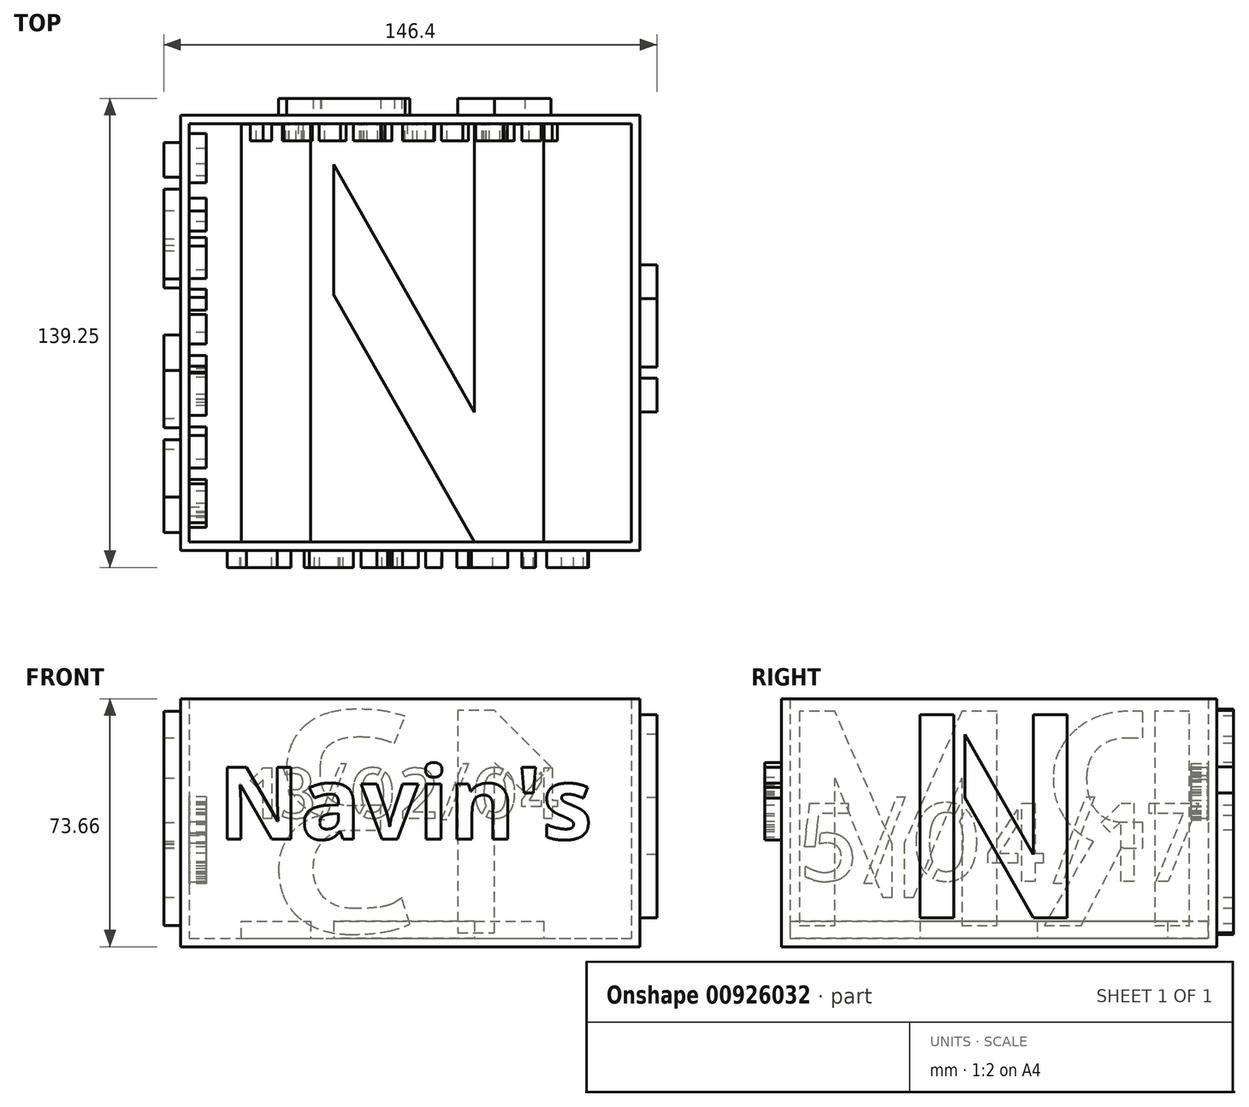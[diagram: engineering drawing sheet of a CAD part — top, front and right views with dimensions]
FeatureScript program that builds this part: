
annotation { "Feature Type Name" : "Feature", "Feature Type Description" : "" }
export const myFeature = defineFeature(function(context is Context, id is Id, definition is map)
    precondition{}
    {
        {
            var Q0;
            Q0=qCreatedBy(makeId("Top.planeOp"),FACE);
            var sketch = newSketch(context, id + "F0", { "sketchPlane" : qUnion([Q0])});
            skLineSegment(sketch, "E0.bottom", {"start": v(-70.44, 64.66) * mm, "end": v(65.96, 64.66) * mm});
            skLineSegment(sketch, "E0.top", {"start": v(-70.44, -64.6) * mm, "end": v(65.96, -64.6) * mm});
            skLineSegment(sketch, "E0.left", {"start": v(-70.44, 64.66) * mm, "end": v(-70.44, -64.6) * mm});
            skLineSegment(sketch, "E0.right", {"start": v(65.96, 64.66) * mm, "end": v(65.96, -64.6) * mm});
            skSolve(sketch);
        }
        {
            var Q0;
            Q0=makeQuery(id+"F0.imprint","IMPRINT",FACE,{"disambiguationData":[TD([[makeQuery(id+"F0.imprint","IMPRINT",EDGE,{"derivedFrom":sQuery(id+"F0.wireOp",EDGE,"E0.bottom")}),-1.0]])]});
            extrude(context, id + "F1", {"entities" : qUnion([Q0]), "depth" : 73.66 * mm, "offsetDistance" : 25.4 * mm});
        }
        {
            var Q0;
            Q0=makeQuery(id+"F1.opExtrude","CAP_FACE",FACE,{"disambiguationData":[OSD([sQuery(id+"F0.wireOp",EDGE,"E0.bottom"),sQuery(id+"F0.wireOp",EDGE,"E0.top"),sQuery(id+"F0.wireOp",EDGE,"E0.left"),sQuery(id+"F0.wireOp",EDGE,"E0.right")])],"isStart":false});
            shell(context, id + "F2", {"entities" : qUnion([Q0]), "thickness" : 2.54 * mm});
        }
        {
            var Q0;
            Q0=makeQuery(id+"F1.opExtrude","SWEPT_FACE",FACE,{"disambiguationData":[OSD([sQuery(id+"F0.wireOp",EDGE,"E0.top")])]});
            var sketch = newSketch(context, id + "F3", { "sketchPlane" : qUnion([Q0])});
            skText(sketch, "E1", { "text": "Navin\'s", "fontName": "OpenSans-Bold.ttf"});
            const initialGuessF3  = {"E1": [-0.0593, 0.03196, 1, 0, 0.02155]};
            skSetInitialGuess(sketch, initialGuessF3);
            skSolve(sketch);
        }
        {
            var Q0;
            Q0 = qSketchRegion(id + "F3", true);
            extrude(context, id + "F4", {"entities" : qUnion([Q0]), "operationType" : NewBodyOperationType.ADD, "depth" : 5 * mm, "offsetDistance" : 25.4 * mm});
        }
        {
            var Q0;
            Q0=makeQuery(id+"F2.opShell","OFFSET_FACE",FACE,{"disambiguationData":[OSD([sQuery(id+"F0.wireOp",EDGE,"E0.bottom"),sQuery(id+"F0.wireOp",EDGE,"E0.top"),sQuery(id+"F0.wireOp",EDGE,"E0.left"),sQuery(id+"F0.wireOp",EDGE,"E0.right")])]});
            var sketch = newSketch(context, id + "F5", { "sketchPlane" : qUnion([Q0])});
            skText(sketch, "E2", { "text": "N", "fontName": "AllertaStencil-Regular.ttf"});
            const initialGuessF5  = {"E2": [-0.0679, -0.06205, 1, 0, 0.12417]};
            skSetInitialGuess(sketch, initialGuessF5);
            skSolve(sketch);
        }
        {
            var Q0;
            Q0 = qSketchRegion(id + "F5", true);
            extrude(context, id + "F6", {"entities" : qUnion([Q0]), "operationType" : NewBodyOperationType.ADD, "depth" : 5 * mm, "offsetDistance" : 25.4 * mm});
        }
        {
            var Q0;
            Q0=makeQuery(id+"F1.opExtrude","SWEPT_FACE",FACE,{"disambiguationData":[OSD([sQuery(id+"F0.wireOp",EDGE,"E0.right")])]});
            var sketch = newSketch(context, id + "F7", { "sketchPlane" : qUnion([Q0])});
            skText(sketch, "E3", { "text": "N", "fontName": "AllertaStencil-Regular.ttf"});
            const initialGuessF7  = {"E3": [-0.03094, 0.00857, 1, 0, 0.06038]};
            skSetInitialGuess(sketch, initialGuessF7);
            skSolve(sketch);
        }
        {
            var Q0;
            Q0 = qSketchRegion(id + "F7", true);
            extrude(context, id + "F8", {"entities" : qUnion([Q0]), "operationType" : NewBodyOperationType.ADD, "depth" : 5 * mm, "offsetDistance" : 25.4 * mm});
        }
        {
            var Q0;
            Q0=makeQuery(id+"F1.opExtrude","SWEPT_FACE",FACE,{"disambiguationData":[OSD([sQuery(id+"F0.wireOp",EDGE,"E0.bottom")])]});
            var sketch = newSketch(context, id + "F9", { "sketchPlane" : qUnion([Q0])});
            skText(sketch, "E4", { "text": "13 ", "fontName": "AllertaStencil-Regular.ttf"});
            const initialGuessF9  = {"E4": [-0.04212, 0.0041, 1, 0, 0.0661]};
            skSetInitialGuess(sketch, initialGuessF9);
            skSolve(sketch);
        }
        {
            var Q0;
            Q0=makeQuery(id+"F9.imprint","IMPRINT",FACE,{"disambiguationData":[TD([[makeQuery(id+"F9.imprint","IMPRINT",EDGE,{"derivedFrom":sQuery(id+"F9.wireOp",EDGE,"E4.sketch_text.stroke-7")}),-1.0]])]});
            var Q1;
            Q1=makeQuery(id+"F9.imprint","IMPRINT",FACE,{"disambiguationData":[TD([[makeQuery(id+"F9.imprint","IMPRINT",EDGE,{"derivedFrom":sQuery(id+"F9.wireOp",EDGE,"E4.sketch_text.stroke-0")}),-1.0]])]});
            extrude(context, id + "F10", {"entities" : qUnion([Q0, Q1]), "operationType" : NewBodyOperationType.ADD, "depth" : 5 * mm, "offsetDistance" : 25.4 * mm});
        }
        {
            var Q0;
            Q0=makeQuery(id+"F1.opExtrude","SWEPT_FACE",FACE,{"disambiguationData":[OSD([sQuery(id+"F0.wireOp",EDGE,"E0.left")])]});
            var sketch = newSketch(context, id + "F11", { "sketchPlane" : qUnion([Q0])});
            skText(sketch, "E5", { "text": "RM", "fontName": "AllertaStencil-Regular.ttf"});
            const initialGuessF11  = {"E5": [-0.06437, 0.00633, 1, 0, 0.06361]};
            skSetInitialGuess(sketch, initialGuessF11);
            skSolve(sketch);
        }
        {
            var Q0;
            Q0 = qSketchRegion(id + "F11", true);
            extrude(context, id + "F12", {"entities" : qUnion([Q0]), "operationType" : NewBodyOperationType.ADD, "depth" : 5 * mm, "offsetDistance" : 25.4 * mm});
        }
        {
            var Q0;
            Q0=makeQuery(id+"F2.opShell","OFFSET_FACE",FACE,{"disambiguationData":[OSD([sQuery(id+"F0.wireOp",EDGE,"E0.bottom")])]});
            var sketch = newSketch(context, id + "F13", { "sketchPlane" : qUnion([Q0])});
            skText(sketch, "E6", { "text": "13/02/04", "fontName": "AllertaStencil-Regular.ttf"});
            const initialGuessF13  = {"E6": [-0.05037, 0.03808, 1, 0, 0.01504]};
            skSetInitialGuess(sketch, initialGuessF13);
            skSolve(sketch);
        }
        {
            var Q0;
            Q0 = qSketchRegion(id + "F13", true);
            extrude(context, id + "F14", {"entities" : qUnion([Q0]), "operationType" : NewBodyOperationType.ADD, "depth" : 5 * mm, "offsetDistance" : 25.4 * mm});
        }
        {
            var Q0;
            Q0=makeQuery(id+"F2.opShell","OFFSET_FACE",FACE,{"disambiguationData":[OSD([sQuery(id+"F0.wireOp",EDGE,"E0.left")])]});
            var sketch = newSketch(context, id + "F15", { "sketchPlane" : qUnion([Q0])});
            skText(sketch, "E7", { "text": "5/04/17", "fontName": "AllertaStencil-Regular.ttf"});
            const initialGuessF15  = {"E7": [-0.06014, 0.01942, 1, 0, 0.0232]};
            skSetInitialGuess(sketch, initialGuessF15);
            skSolve(sketch);
        }
        {
            var Q0;
            Q0 = qSketchRegion(id + "F15", true);
            extrude(context, id + "F16", {"entities" : qUnion([Q0]), "operationType" : NewBodyOperationType.ADD, "depth" : 5 * mm, "offsetDistance" : 25.4 * mm});
        }
    });
